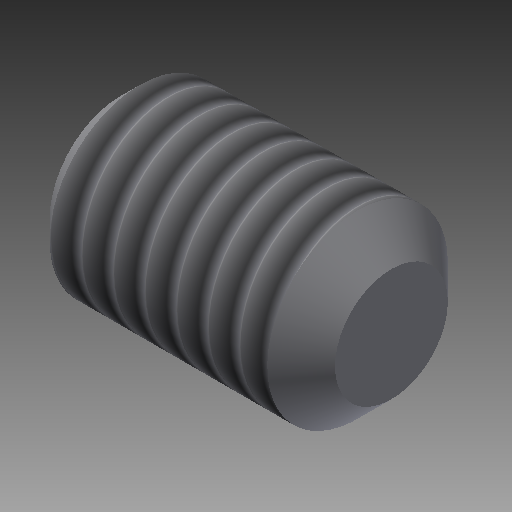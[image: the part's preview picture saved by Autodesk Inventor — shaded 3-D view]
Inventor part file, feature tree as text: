
AUTODESK INVENTOR PART (.ipt)
format: ipt  version: 2019 (Build 230136000, 136)  size: 211,968 bytes
history: native  units: mm
features: other x7, sketch x3, revolve x2, thread x1, extrude x1
ambient origin geometry x8: Origin, YZ Plane, XZ Plane, XY Plane, X Axis, Y Axis, Z Axis, Center Point
bodies: Solid1 (feature_tree)
feature tree (14):
  revolve  "Revolution1"  [1 undecoded]
  thread  "Thread1"  [1 undecoded]
  extrude  "Extrusion1"  TaperAngle=0.0deg  [1 undecoded]
  revolve  "Revolution2"  [1 undecoded]
  other  "CP_XY"
  other  "CP_YZ"
  other  "CP_ZX"
  other  "CP_X"
  other  "CP_Y"
  other  "CP_Z"
  other  "CP_Center"
  sketch  "Sketch_1"  dims[d0=360.0deg d1=4.8205mm d2=0.0mm d3=1.5mm d4=0.0mm]
  sketch  "Sketch_2"  dims[d5=360.0deg d6=0.0mm]
  sketch  "Sketch_3"
note: 4 required parameter values undecoded (feature->parameter linkage not recoverable at this tier; creation-order binding heuristic only, values carry confidence <= 0.55)